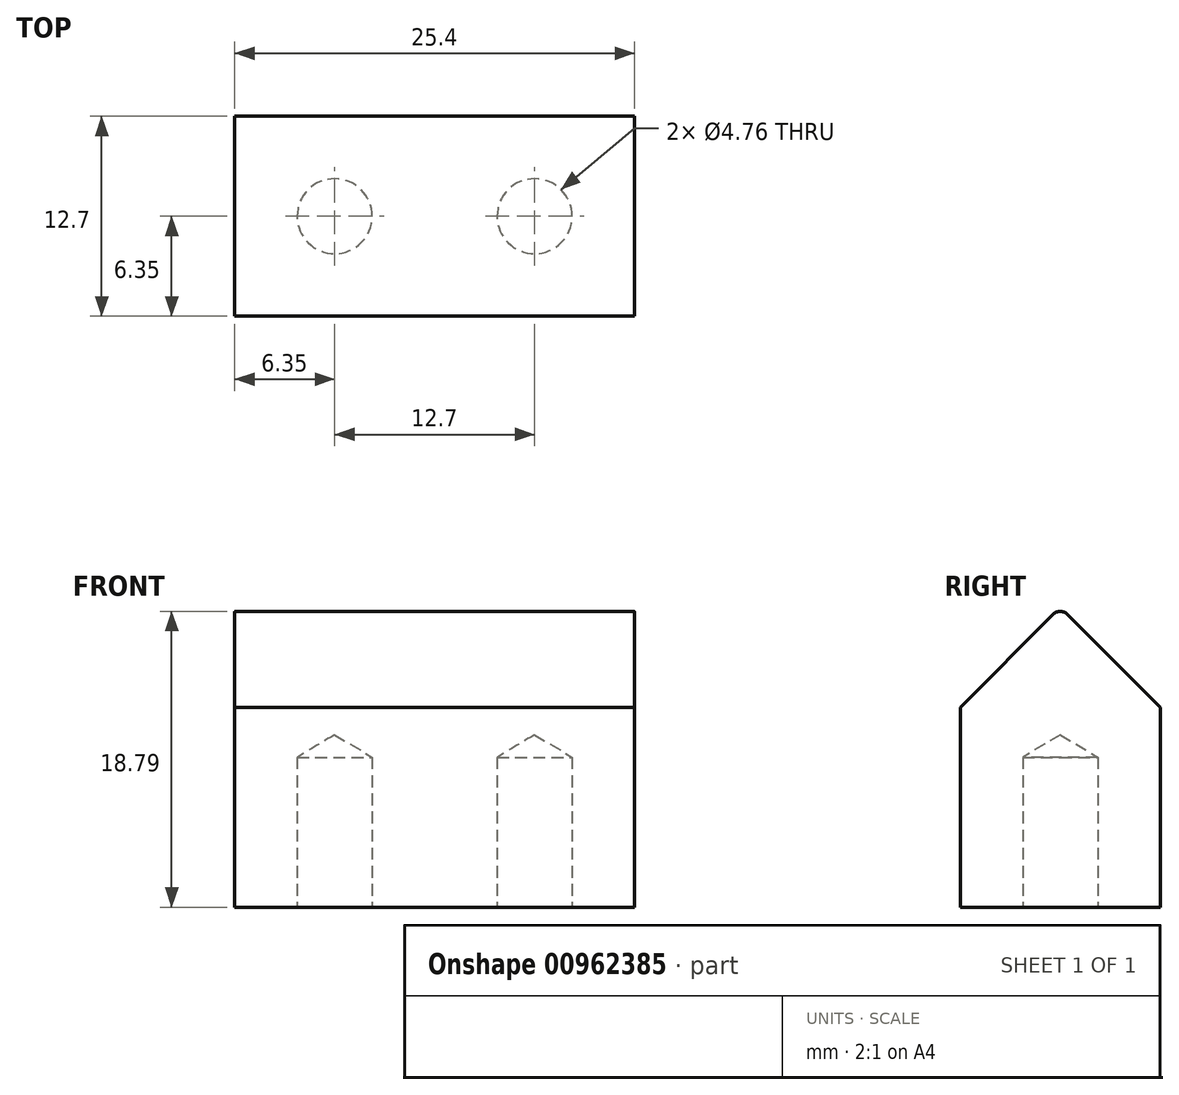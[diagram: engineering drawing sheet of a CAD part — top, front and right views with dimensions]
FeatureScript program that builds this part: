
annotation { "Feature Type Name" : "Feature", "Feature Type Description" : "" }
export const myFeature = defineFeature(function(context is Context, id is Id, definition is map)
    precondition{}
    {
        {
            var Q0;
            Q0=qCreatedBy(makeId("Right.planeOp"),FACE);
            var sketch = newSketch(context, id + "F0", { "sketchPlane" : qUnion([Q0])});
            skLineSegment(sketch, "E0.bottom", {"start": v(0, 0) * mm, "end": v(12.7, 0) * mm});
            skLineSegment(sketch, "E0.top", {"start": v(0, 12.7) * mm, "end": v(12.7, 12.7) * mm});
            skLineSegment(sketch, "E0.left", {"start": v(0, 0) * mm, "end": v(0, 12.7) * mm});
            skLineSegment(sketch, "E0.right", {"start": v(12.7, 0) * mm, "end": v(12.7, 12.7) * mm});
            skLineSegment(sketch, "E1", {"start": v(0, 12.7) * mm, "end": v(6.35, 19.05) * mm});
            skLineSegment(sketch, "E2", {"start": v(12.7, 12.7) * mm, "end": v(6.35, 19.05) * mm});
            skPoint(sketch, "E3.orphan", {"position": v(0, 25.4) * mm});
            skPoint(sketch, "E4.orphan", {"position": v(12.7, 25.4) * mm});
            skSolve(sketch);
        }
        {
            var Q0;
            Q0 = qSketchRegion(id + "F0", true);
            extrude(context, id + "F1", {"entities" : qUnion([Q0]), "depth" : 25.4 * mm, "offsetDistance" : 25.4 * mm});
        }
        {
            var Q0;
            Q0=makeQuery(id+"F1.opExtrude","SWEPT_FACE",FACE,{"disambiguationData":[OSD([sQuery(id+"F0.wireOp",EDGE,"E0.bottom")])]});
            var sketch = newSketch(context, id + "F2", { "sketchPlane" : qUnion([Q0])});
            skCircle(sketch, "E5", {"center": v(6.35, -6.35) * mm, "radius": 2.38 * mm});
            skCircle(sketch, "E6", {"center": v(19.05, -6.35) * mm, "radius": 2.38 * mm});
            skSolve(sketch);
        }
        {
            var Q0;
            Q0=sQuery(id+"F2.wireOp",VERTEX,"E5.center");
            var Q1;
            Q1=sQuery(id+"F2.wireOp",VERTEX,"E6.center");
            var Q2;
            Q2=makeQuery(id+"F1.opExtrude","SWEPT_BODY",BODY,{"disambiguationData":[OSD([sQuery(id+"F0.wireOp",EDGE,"E0.bottom"),sQuery(id+"F0.wireOp",EDGE,"E0.left"),sQuery(id+"F0.wireOp",EDGE,"E0.right"),sQuery(id+"F0.wireOp",EDGE,"E1"),sQuery(id+"F0.wireOp",EDGE,"E2")])]});
            hole(context, id + "F3", {"style" : HoleStyle.SIMPLE, "endStyle" : HoleEndStyle.BLIND, "holeDiameter" : 4.76 * mm, "majorDiameter" : 6.35 * mm, "holeDepth" : 9.52 * mm, "isTappedThrough" : true, "tappedDepth" : 12.7 * mm, "tapClearance" : 3, "startFromSketch" : true, "locations" : qUnion([Q0, Q1]), "scope" : qUnion([Q2])});
        }
        {
            var Q0;
            Q0=makeQuery(id+"F1.opExtrude","SWEPT_EDGE",EDGE,{"disambiguationData":[OSD([sQuery(id+"F0.wireOp",EDGE,"E1"),sQuery(id+"F0.wireOp",EDGE,"E2")])]});
            fillet(context, id + "F4", {"entities" : qUnion([Q0]), "radius" : 0.64 * mm, "tangentPropagation" : true, "allowEdgeOverflow" : false});
        }
    });
